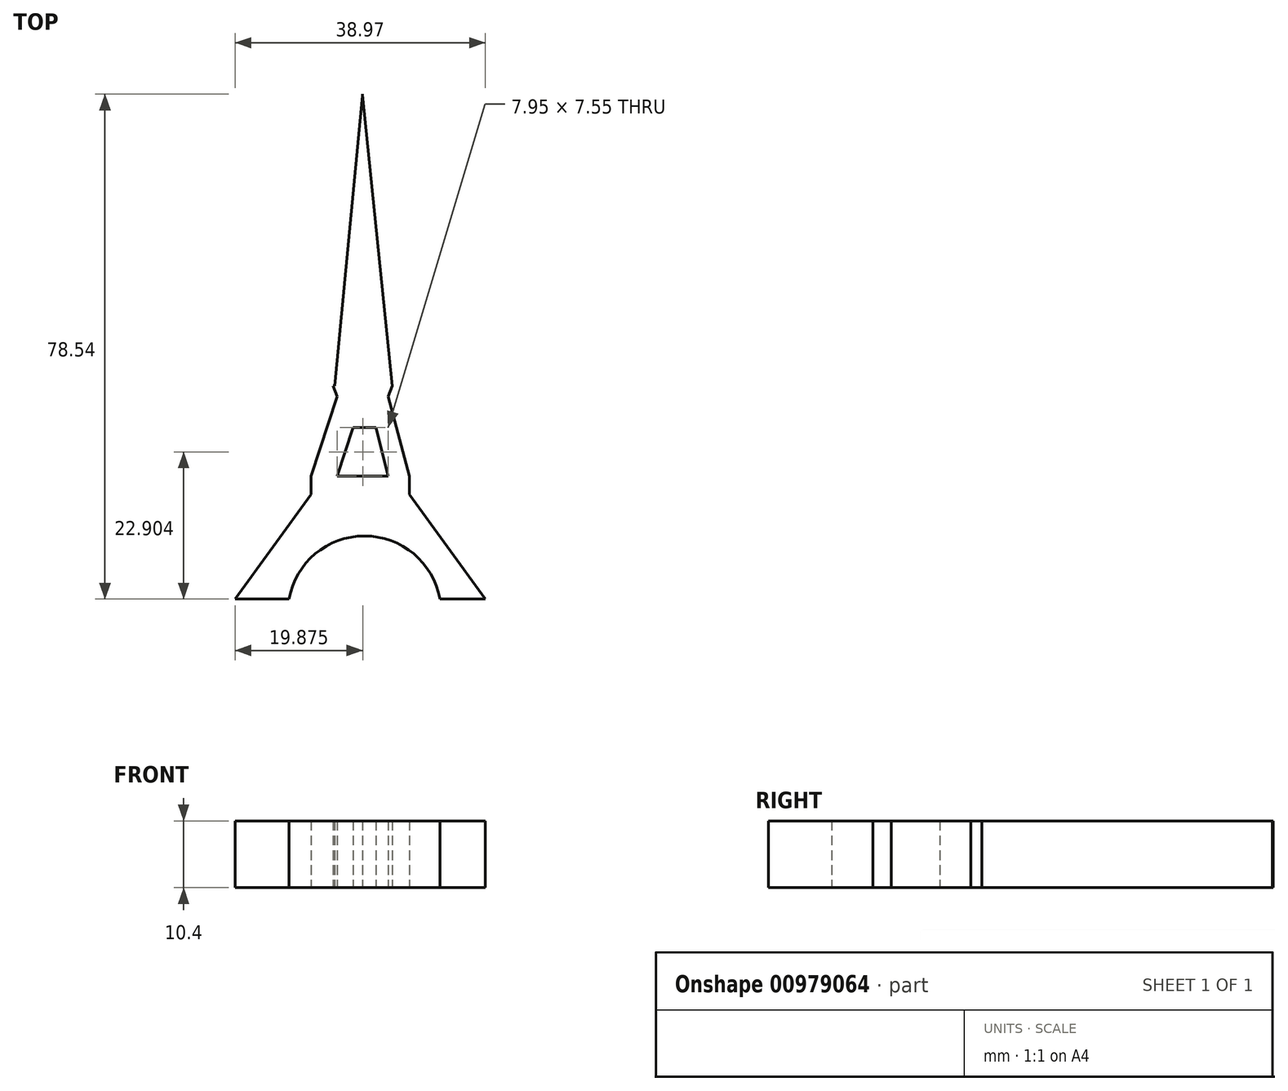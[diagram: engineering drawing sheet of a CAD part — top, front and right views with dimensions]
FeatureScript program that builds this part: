
annotation { "Feature Type Name" : "Feature", "Feature Type Description" : "" }
export const myFeature = defineFeature(function(context is Context, id is Id, definition is map)
    precondition{}
    {
        {
            var Q0;
            Q0=qCreatedBy(makeId("Top.planeOp"),FACE);
            var sketch = newSketch(context, id + "F0", { "sketchPlane" : qUnion([Q0])});
            skLineSegment(sketch, "E0", {"start": v(-15.9, -49.82) * mm, "end": v(-7.5, -49.82) * mm});
            skLineSegment(sketch, "E1", {"start": v(11.25, -33.55) * mm, "end": v(23.07, -49.82) * mm});
            skPoint(sketch, "E2.start.orphan", {"position": v(-4.08, -33.55) * mm});
            skLineSegment(sketch, "E3", {"start": v(-15.9, -49.82) * mm, "end": v(-4.08, -33.55) * mm});
            skLineSegment(sketch, "E4", {"start": v(-4.08, -33.55) * mm, "end": v(11.25, -33.55) * mm});
            skArc(sketch, "E5", {"start": v(16, -49.82) * mm, "mid": v(4.25, -40) * mm, "end": v(-7.5, -49.82) * mm});
            skLineSegment(sketch, "E6.trimOffspring", {"start": v(16, -49.82) * mm, "end": v(23.07, -49.82) * mm});
            skLineSegment(sketch, "E7", {"start": v(-4.08, -30.7) * mm, "end": v(11.25, -30.7) * mm});
            skLineSegment(sketch, "E8", {"start": v(-4.08, -30.7) * mm, "end": v(-4.08, -33.55) * mm});
            skLineSegment(sketch, "E9", {"start": v(11.25, -30.7) * mm, "end": v(11.25, -33.55) * mm});
            skLineSegment(sketch, "E10", {"start": v(3.92, 28.72) * mm, "end": v(4.25, -51.94) * mm});
            skLineSegment(sketch, "E11", {"start": v(-4.08, -30.7) * mm, "end": v(0, -18.34) * mm});
            skLineSegment(sketch, "E12", {"start": v(11.25, -30.7) * mm, "end": v(7.95, -18.34) * mm});
            skLineSegment(sketch, "E13", {"start": v(0, -18.34) * mm, "end": v(7.95, -18.34) * mm});
            skLineSegment(sketch, "E14", {"start": v(3.91, 28.6) * mm, "end": v(3.92, 28.72) * mm});
            skLineSegment(sketch, "E15", {"start": v(3.93, 28.6) * mm, "end": v(3.92, 28.72) * mm});
            skLineSegment(sketch, "E16", {"start": v(0, -30.7) * mm, "end": v(7.95, -30.7) * mm});
            skLineSegment(sketch, "E17", {"start": v(0, -30.7) * mm, "end": v(2.49, -23.15) * mm});
            skLineSegment(sketch, "E18", {"start": v(2.49, -23.15) * mm, "end": v(6.04, -23.14) * mm});
            skLineSegment(sketch, "E19", {"start": v(6.04, -23.14) * mm, "end": v(7.95, -30.7) * mm});
            skLineSegment(sketch, "E20", {"start": v(2.49, 28.72) * mm, "end": v(3.93, 28.6) * mm});
            skPoint(sketch, "E21.orphan", {"position": v(6.04, 28.43) * mm});
            skLineSegment(sketch, "E22", {"start": v(4.1, -16.64) * mm, "end": v(8.58, -16.64) * mm});
            skLineSegment(sketch, "E23", {"start": v(3.92, 28.5) * mm, "end": v(3.93, 28.6) * mm});
            skLineSegment(sketch, "E24", {"start": v(3.93, 28.6) * mm, "end": v(8.58, -16.64) * mm});
            skLineSegment(sketch, "E25", {"start": v(7.95, -18.34) * mm, "end": v(8.58, -16.64) * mm});
            skPoint(sketch, "E26.start.orphan", {"position": v(0, -16.64) * mm});
            skPoint(sketch, "E27.MirrorCS.end.orphan", {"position": v(-0.37, -16.68) * mm});
            skPoint(sketch, "E27.MirrorCS.start.orphan", {"position": v(3.91, 28.6) * mm});
            skLineSegment(sketch, "E28", {"start": v(4.1, -16.64) * mm, "end": v(0, -16.64) * mm});
            skLineSegment(sketch, "E29", {"start": v(0, -18.34) * mm, "end": v(-0.64, -16.64) * mm});
            skLineSegment(sketch, "E30", {"start": v(-0.64, -16.64) * mm, "end": v(0, -16.64) * mm});
            skLineSegment(sketch, "E31", {"start": v(3.93, 28.6) * mm, "end": v(-0.37, -16.68) * mm});
            skSolve(sketch);
        }
        {
            var Q0;
            Q0 = qSketchRegion(id + "F0", true);
            extrude(context, id + "F1", {"entities" : qUnion([Q0]), "depth" : 10.4 * mm, "offsetDistance" : 25 * mm});
        }
    });
